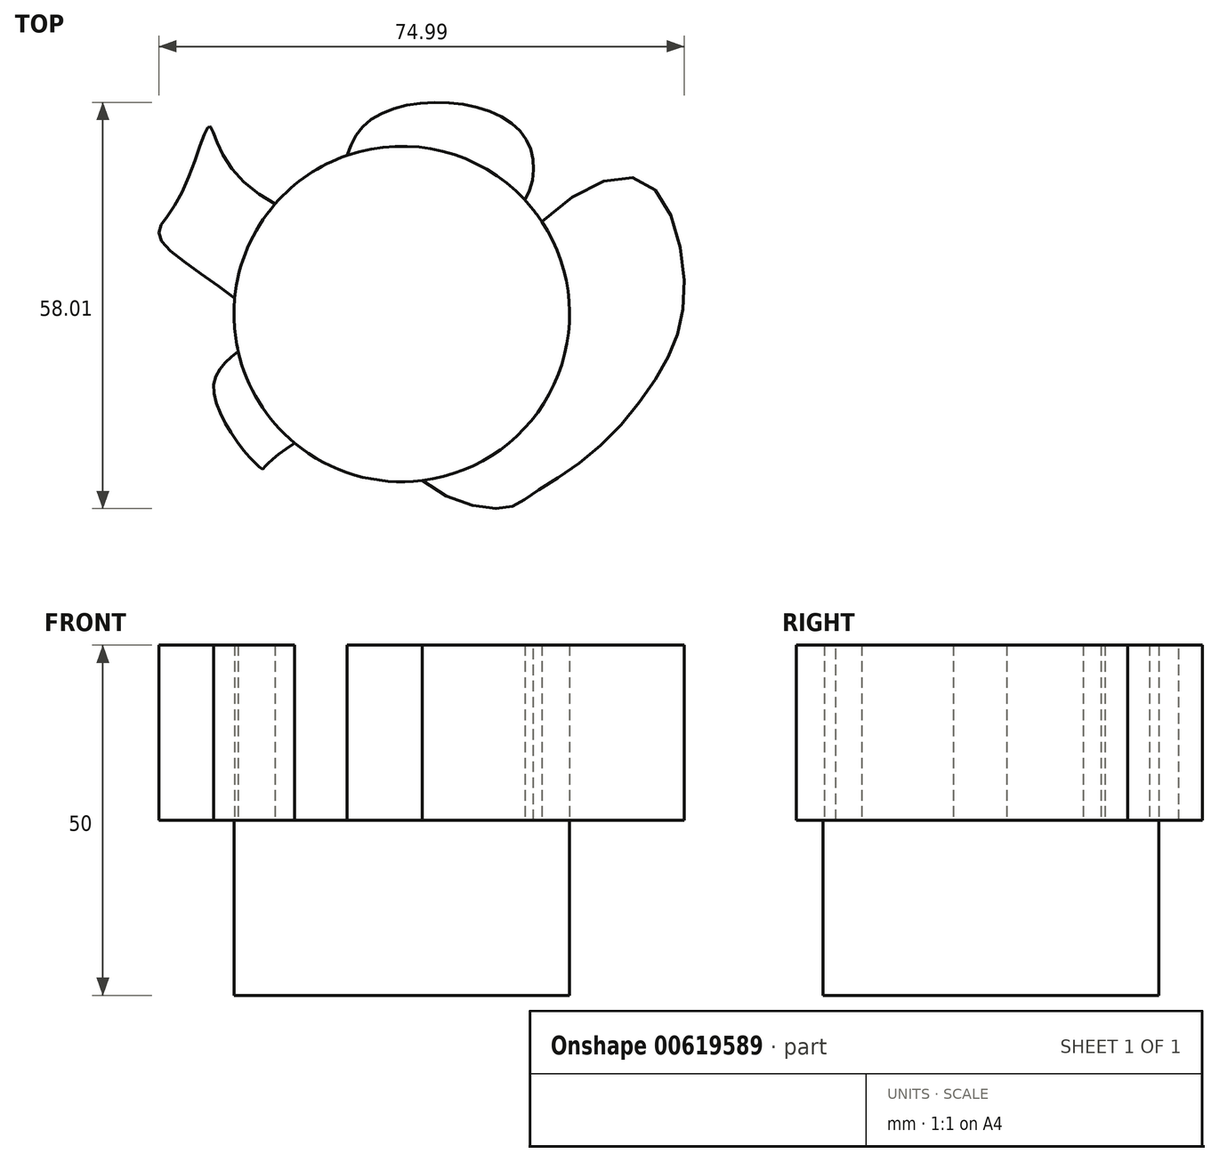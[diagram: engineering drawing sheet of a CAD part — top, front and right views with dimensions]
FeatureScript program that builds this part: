
annotation { "Feature Type Name" : "Feature", "Feature Type Description" : "" }
export const myFeature = defineFeature(function(context is Context, id is Id, definition is map)
    precondition{}
    {
        {
            var Q0;
            Q0=qCreatedBy(makeId("Top.planeOp"),FACE);
            var sketch = newSketch(context, id + "F0", { "sketchPlane" : qUnion([Q0])});
            skCircle(sketch, "E0", {"center": v(0, 0) * mm, "radius": 23.95 * mm});
            skSolve(sketch);
        }
        {
            var Q0;
            Q0=makeQuery(id+"F0.imprint","IMPRINT",FACE,{"disambiguationData":[TD([[makeQuery(id+"F0.imprint","IMPRINT",EDGE,{"derivedFrom":sQuery(id+"F0.wireOp",EDGE,"E0")}),1.0]])]});
            extrude(context, id + "F1", {"entities" : qUnion([Q0]), "depth" : 25 * mm, "offsetDistance" : 25 * mm});
        }
        {
            var Q0;
            Q0=makeQuery(id+"F1.opExtrude","CAP_FACE",FACE,{"disambiguationData":[OSD([sQuery(id+"F0.wireOp",EDGE,"E0")])],"isStart":false});
            var sketch = newSketch(context, id + "F2", { "sketchPlane" : qUnion([Q0])});
            skFitSpline(sketch, "E1", {"points": [v(-24.72, 21.33) * mm, v(-10.8, 14.38) * mm, v(-5.54, 26.78) * mm, v(16.63, 26.4) * mm, v(14.94, 13.44) * mm, v(-2.54, 9.12) * mm, v(-4.6, 1.6) * mm, v(-4.98, -7.42) * mm, v(3.48, -7.42) * mm, v(10.62, -4.98) * mm, v(15.5, 7.61) * mm, v(33.74, 19.26) * mm, v(40.31, 4.04) * mm, v(36.93, -8.18) * mm, v(26.97, -20.02) * mm, v(18.14, -26.03) * mm, v(14.57, -27.72) * mm, v(2.9, -23.78) * mm, v(-6.3, -15.13) * mm, v(-19.45, -21.7) * mm, v(-20.02, -22.08) * mm, v(-26.78, -9.68) * mm, v(-20.58, -1.79) * mm, v(-34.3, 10.43) * mm, v(-32.05, 16.07) * mm, v(-27.53, 26.78) * mm, v(-24.72, 21.33) * mm]});
            skSolve(sketch);
        }
        {
            var Q0;
            {var subQ0=sQuery(id+"F2.wireOp",EDGE,"E1");var subQ1=makeQuery(id+"F1.opExtrude","CAP_EDGE",EDGE,{"disambiguationData":[OSD([sQuery(id+"F0.wireOp",EDGE,"E0")])],"isStart":false});var subQ2=makeQuery(id+"F2.imprint","INTERSECT",VERTEX,{"disambiguationData":[OD(1.0)],"derivedFrom":[subQ1,subQ0]});Q0=makeQuery(id+"F2.imprint","IMPRINT",FACE,{"disambiguationData":[TD([[makeQuery(id+"F2.imprint","IMPRINT",EDGE,{"disambiguationData":[TD([[subQ2,1.0]])],"derivedFrom":subQ0}),-1.0]])]});}
            var Q1;
            {var subQ0=sQuery(id+"F2.wireOp",EDGE,"E1");var subQ1=makeQuery(id+"F1.opExtrude","CAP_EDGE",EDGE,{"disambiguationData":[OSD([sQuery(id+"F0.wireOp",EDGE,"E0")])],"isStart":false});var subQ2=makeQuery(id+"F2.imprint","INTERSECT",VERTEX,{"disambiguationData":[OD(0.0)],"derivedFrom":[subQ1,subQ0]});Q1=makeQuery(id+"F2.imprint","IMPRINT",FACE,{"disambiguationData":[TD([[makeQuery(id+"F2.imprint","IMPRINT",EDGE,{"disambiguationData":[TD([[subQ2,-1.0]])],"derivedFrom":subQ0}),-1.0]])]});}
            var Q2;
            {var subQ0=sQuery(id+"F2.wireOp",EDGE,"E1");var subQ1=makeQuery(id+"F1.opExtrude","CAP_EDGE",EDGE,{"disambiguationData":[OSD([sQuery(id+"F0.wireOp",EDGE,"E0")])],"isStart":false});var subQ2=makeQuery(id+"F2.imprint","INTERSECT",VERTEX,{"disambiguationData":[OD(3.0)],"derivedFrom":[subQ1,subQ0]});Q2=makeQuery(id+"F2.imprint","IMPRINT",FACE,{"disambiguationData":[TD([[makeQuery(id+"F2.imprint","IMPRINT",EDGE,{"disambiguationData":[TD([[subQ2,-1.0]])],"derivedFrom":subQ0}),-1.0]])]});}
            var Q3;
            {var subQ0=sQuery(id+"F2.wireOp",EDGE,"E1");var subQ1=makeQuery(id+"F1.opExtrude","CAP_EDGE",EDGE,{"disambiguationData":[OSD([sQuery(id+"F0.wireOp",EDGE,"E0")])],"isStart":false});var subQ2=makeQuery(id+"F2.imprint","INTERSECT",VERTEX,{"disambiguationData":[OD(5.0)],"derivedFrom":[subQ1,subQ0]});Q3=makeQuery(id+"F2.imprint","IMPRINT",FACE,{"disambiguationData":[TD([[makeQuery(id+"F2.imprint","IMPRINT",EDGE,{"disambiguationData":[TD([[subQ2,-1.0]])],"derivedFrom":subQ0}),-1.0]])]});}
            extrude(context, id + "F3", {"entities" : qUnion([Q0, Q1, Q2, Q3]), "depth" : 25 * mm, "offsetDistance" : 25 * mm});
        }
    });
